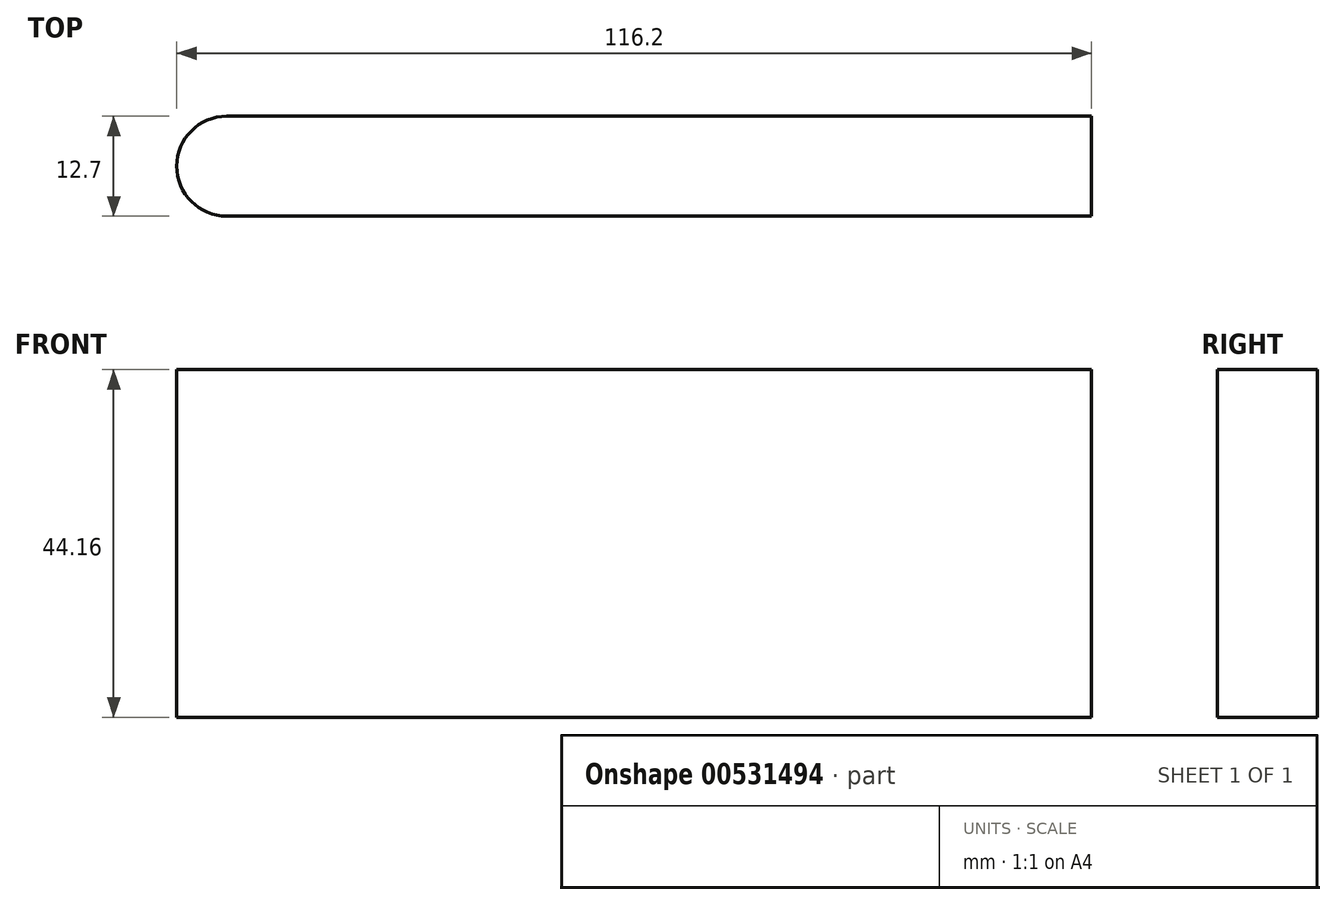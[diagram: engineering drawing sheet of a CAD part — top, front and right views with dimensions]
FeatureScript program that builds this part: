
annotation { "Feature Type Name" : "Feature", "Feature Type Description" : "" }
export const myFeature = defineFeature(function(context is Context, id is Id, definition is map)
    precondition{}
    {
        {
            var Q0;
            Q0=qCreatedBy(makeId("Front.planeOp"),FACE);
            var sketch = newSketch(context, id + "F0", { "sketchPlane" : qUnion([Q0])});
            skLineSegment(sketch, "E0.bottom", {"start": v(58.1, 22.08) * mm, "end": v(-58.1, 22.08) * mm});
            skLineSegment(sketch, "E0.top", {"start": v(58.1, -22.08) * mm, "end": v(-58.1, -22.08) * mm});
            skLineSegment(sketch, "E0.left", {"start": v(58.1, 22.08) * mm, "end": v(58.1, -22.08) * mm});
            skLineSegment(sketch, "E0.right", {"start": v(-58.1, 22.08) * mm, "end": v(-58.1, -22.08) * mm});
            skPoint(sketch, "E0.middle", {"position": v(0, 0) * mm});
            skSolve(sketch);
        }
        {
            var Q0;
            Q0=makeQuery(id+"F0.imprint","IMPRINT",FACE,{"disambiguationData":[TD([[makeQuery(id+"F0.imprint","IMPRINT",EDGE,{"derivedFrom":sQuery(id+"F0.wireOp",EDGE,"E0.bottom")}),1.0]])]});
            extrude(context, id + "F1", {"entities" : qUnion([Q0]), "depth" : 12.7 * mm, "offsetDistance" : 25.4 * mm});
        }
        {
            var Q0;
            Q0=makeQuery(id+"F1.opExtrude","CAP_EDGE",EDGE,{"disambiguationData":[OSD([sQuery(id+"F0.wireOp",EDGE,"E0.right")])],"isStart":true});
            var Q1;
            Q1=makeQuery(id+"F1.opExtrude","CAP_EDGE",EDGE,{"disambiguationData":[OSD([sQuery(id+"F0.wireOp",EDGE,"E0.right")])],"isStart":false});
            fillet(context, id + "F2", {"entities" : qUnion([Q0, Q1]), "radius" : 6.35 * mm, "tangentPropagation" : true, "allowEdgeOverflow" : false});
        }
    });
